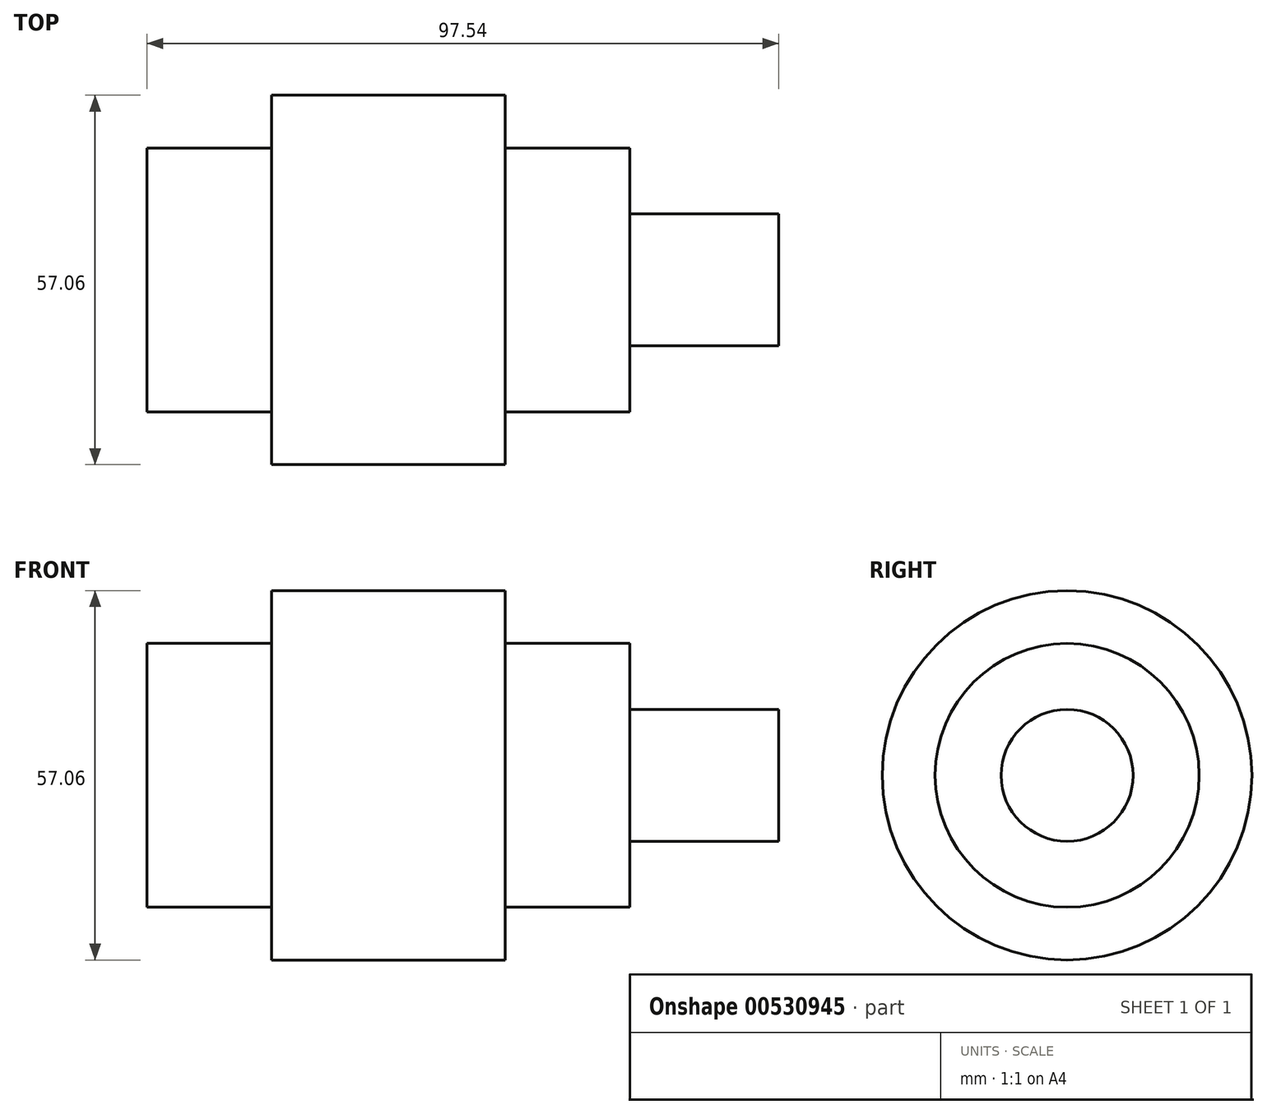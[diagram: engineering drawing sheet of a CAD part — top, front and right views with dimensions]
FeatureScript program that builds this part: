
annotation { "Feature Type Name" : "Feature", "Feature Type Description" : "" }
export const myFeature = defineFeature(function(context is Context, id is Id, definition is map)
    precondition{}
    {
        {
            var Q0;
            Q0=qCreatedBy(makeId("Front.planeOp"),FACE);
            var sketch = newSketch(context, id + "F0", { "sketchPlane" : qUnion([Q0])});
            skLineSegment(sketch, "E0.bottom", {"start": v(0, 0) * mm, "end": v(18.05, 0) * mm});
            skLineSegment(sketch, "E0.top", {"start": v(0, 28.53) * mm, "end": v(18.05, 28.53) * mm});
            skLineSegment(sketch, "E0.left", {"start": v(0, 0) * mm, "end": v(0, 28.53) * mm});
            skLineSegment(sketch, "E0.right", {"start": v(18.05, 0) * mm, "end": v(18.05, 28.53) * mm});
            skLineSegment(sketch, "E1.bottom", {"start": v(18.05, 20.38) * mm, "end": v(37.27, 20.38) * mm});
            skLineSegment(sketch, "E1.top", {"start": v(18.05, 0) * mm, "end": v(37.27, 0) * mm});
            skLineSegment(sketch, "E1.left", {"start": v(18.05, 20.38) * mm, "end": v(18.05, 0) * mm});
            skLineSegment(sketch, "E1.right", {"start": v(37.27, 20.38) * mm, "end": v(37.27, 0) * mm});
            skLineSegment(sketch, "E2.bottom", {"start": v(37.27, 10.19) * mm, "end": v(60.27, 10.19) * mm});
            skLineSegment(sketch, "E2.top", {"start": v(37.27, 0) * mm, "end": v(60.27, 0) * mm});
            skLineSegment(sketch, "E2.left", {"start": v(37.27, 10.19) * mm, "end": v(37.27, 0) * mm});
            skLineSegment(sketch, "E2.right", {"start": v(60.27, 10.19) * mm, "end": v(60.27, 0) * mm});
            skLineSegment(sketch, "E3.MirrorCS", {"start": v(-18.05, 20.38) * mm, "end": v(-18.05, 0) * mm});
            skLineSegment(sketch, "E4.MirrorCS", {"start": v(-18.05, 0) * mm, "end": v(-18.05, 28.53) * mm});
            skLineSegment(sketch, "E5.MirrorCS", {"start": v(0, 28.53) * mm, "end": v(-18.05, 28.53) * mm});
            skLineSegment(sketch, "E6.MirrorCS", {"start": v(-18.05, 20.38) * mm, "end": v(-37.27, 20.38) * mm});
            skLineSegment(sketch, "E7.MirrorCS", {"start": v(-37.27, 20.38) * mm, "end": v(-37.27, 0) * mm});
            skLineSegment(sketch, "E8.MirrorCS", {"start": v(-37.27, 10.19) * mm, "end": v(-37.27, 0) * mm});
            skLineSegment(sketch, "E9.MirrorCS", {"start": v(-37.27, 10.19) * mm, "end": v(-60.27, 10.19) * mm});
            skLineSegment(sketch, "E10.MirrorCS", {"start": v(-60.27, 10.19) * mm, "end": v(-60.27, 0) * mm});
            skLineSegment(sketch, "E11", {"start": v(-63.9, 0) * mm, "end": v(70.9, 0) * mm});
            skPoint(sketch, "E11.endSnap0", {"position": v(48.77, 0) * mm});
            skLineSegment(sketch, "E12", {"start": v(-60.27, 0) * mm, "end": v(-40.32, 0) * mm});
            skSolve(sketch);
        }
        {
            var Q0;
            {var subQ1=sQuery(id+"F0.wireOp",EDGE,"E8.MirrorCS");Q0=makeQuery(id+"F0.imprint","IMPRINT",FACE,{"disambiguationData":[TD([[makeQuery(id+"F0.imprint","IMPRINT",EDGE,{"derivedFrom":subQ1}),-1.0]])]});}
            var Q1;
            {var subQ0=sQuery(id+"F0.wireOp",EDGE,"E6.MirrorCS");Q1=makeQuery(id+"F0.imprint","IMPRINT",FACE,{"disambiguationData":[TD([[makeQuery(id+"F0.imprint","IMPRINT",EDGE,{"derivedFrom":subQ0}),1.0]])]});}
            var Q2;
            {var subQ5=sQuery(id+"F0.wireOp",EDGE,"E0.left");Q2=makeQuery(id+"F0.imprint","IMPRINT",FACE,{"disambiguationData":[TD([[makeQuery(id+"F0.imprint","IMPRINT",EDGE,{"derivedFrom":subQ5}),1.0]])]});}
            var Q3;
            Q3=makeQuery(id+"F0.imprint","IMPRINT",FACE,{"disambiguationData":[TD([[makeQuery(id+"F0.imprint","IMPRINT",EDGE,{"derivedFrom":sQuery(id+"F0.wireOp",EDGE,"E0.top")}),-1.0]])]});
            var Q4;
            Q4=makeQuery(id+"F0.imprint","IMPRINT",FACE,{"disambiguationData":[TD([[makeQuery(id+"F0.imprint","IMPRINT",EDGE,{"derivedFrom":sQuery(id+"F0.wireOp",EDGE,"E1.bottom")}),-1.0]])]});
            var Q5;
            Q5=makeQuery(id+"F0.imprint","IMPRINT",FACE,{"disambiguationData":[TD([[makeQuery(id+"F0.imprint","IMPRINT",EDGE,{"derivedFrom":sQuery(id+"F0.wireOp",EDGE,"E2.bottom")}),-1.0]])]});
            var Q6;
            Q6=sQuery(id+"F0.wireOp",EDGE,"E11");
            revolve(context, id + "F1", {"entities" : qUnion([Q0, Q1, Q2, Q3, Q4, Q5]), "axis" : qUnion([Q6]), "revolveType" : RevolveType.FULL});
        }
    });
